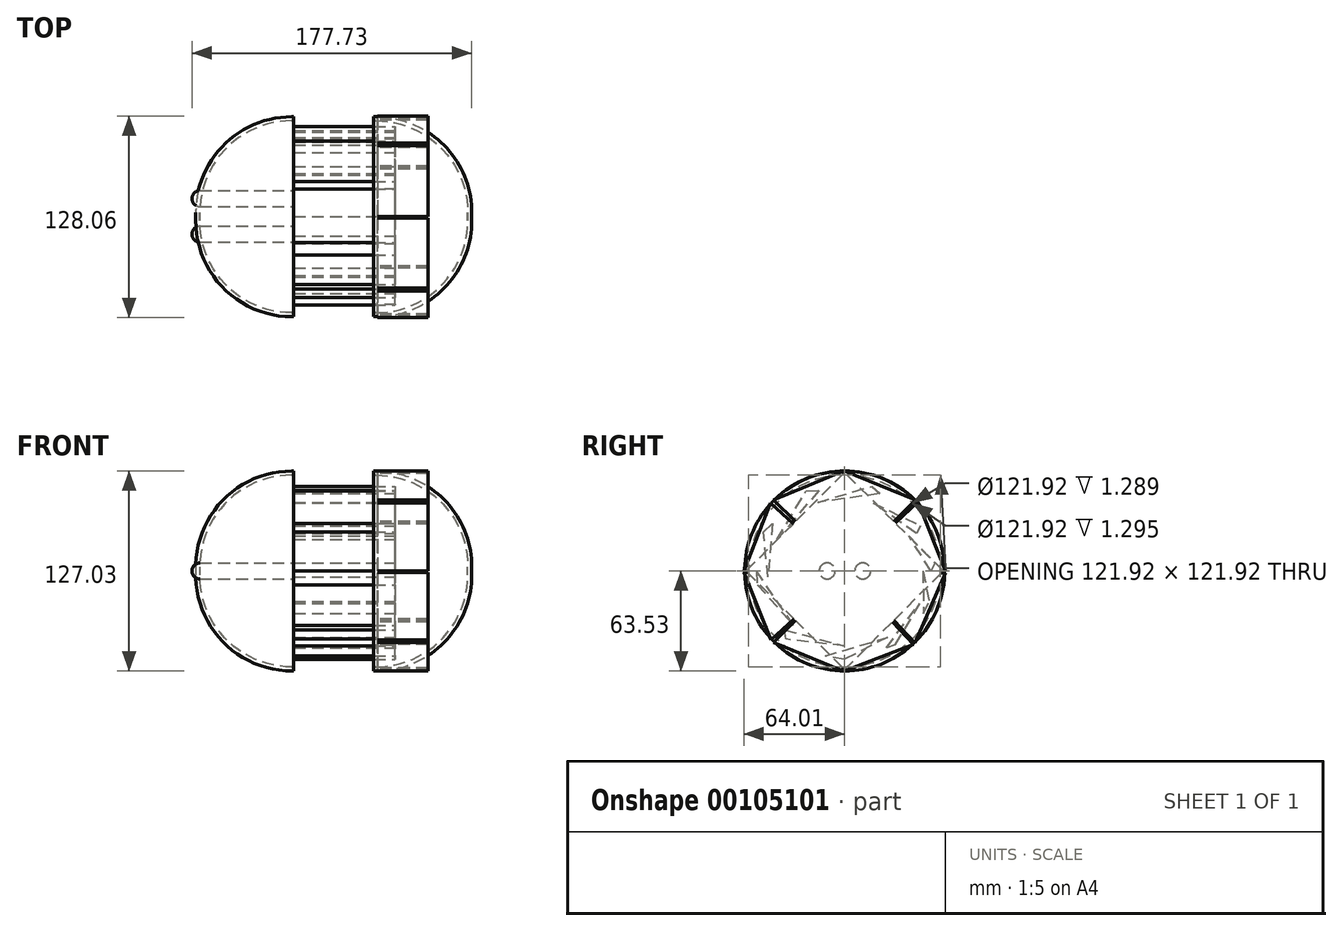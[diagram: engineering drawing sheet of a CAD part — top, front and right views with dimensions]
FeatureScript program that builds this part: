
annotation { "Feature Type Name" : "Feature", "Feature Type Description" : "" }
export const myFeature = defineFeature(function(context is Context, id is Id, definition is map)
    precondition{}
    {
        {
            var Q0;
            Q0=qCreatedBy(makeId("Right.planeOp"),FACE);
            var sketch = newSketch(context, id + "F0", { "sketchPlane" : qUnion([Q0])});
            skCircle(sketch, "E0", {"center": v(0, 0) * mm, "radius": 63.5 * mm});
            skSolve(sketch);
        }
        {
            var Q0;
            Q0=makeQuery(id+"F0.imprint","IMPRINT",FACE,{"disambiguationData":[TD([[makeQuery(id+"F0.imprint","IMPRINT",EDGE,{"derivedFrom":sQuery(id+"F0.wireOp",EDGE,"E0")}),1.0]])]});
            extrude(context, id + "F1", {"entities" : qUnion([Q0]), "depth" : 62.25 * mm});
        }
        {
            var Q0;
            Q0=makeQuery(id+"F1.opExtrude","CAP_FACE",FACE,{"disambiguationData":[OSD([sQuery(id+"F0.wireOp",EDGE,"E0")])],"isStart":false});
            fillet(context, id + "F2", {"entities" : qUnion([Q0]), "radius" : 60.96 * mm, "tangentPropagation" : true, "allowEdgeOverflow" : false});
        }
        {
            var Q0;
            Q0=makeQuery(id+"F1.opExtrude","CAP_FACE",FACE,{"disambiguationData":[OSD([sQuery(id+"F0.wireOp",EDGE,"E0")])],"isStart":true});
            shell(context, id + "F3", {"entities" : qUnion([Q0]), "thickness" : 2.54 * mm});
        }
        {
            var Q0;
            Q0=qCreatedBy(makeId("Right.planeOp"),FACE);
            var sketch = newSketch(context, id + "F4", { "sketchPlane" : qUnion([Q0])});
            skLineSegment(sketch, "E1", {"start": v(0, -56.04) * mm, "end": v(-12.28, -54.03) * mm});
            skLineSegment(sketch, "E2", {"start": v(-12.28, -54.03) * mm, "end": v(27.32, -42.1) * mm});
            skLineSegment(sketch, "E3", {"start": v(27.32, -42.1) * mm, "end": v(0, -56.04) * mm});
            skLineSegment(sketch, "E4", {"start": v(31.88, -46.96) * mm, "end": v(26.45, -48.8) * mm});
            skLineSegment(sketch, "E5", {"start": v(26.45, -48.8) * mm, "end": v(47.54, -20.5) * mm});
            skLineSegment(sketch, "E6", {"start": v(47.54, -20.5) * mm, "end": v(31.88, -46.96) * mm});
            skLineSegment(sketch, "E7", {"start": v(57.24, 5.09) * mm, "end": v(54.8, 0) * mm});
            skLineSegment(sketch, "E8", {"start": v(54.8, 0) * mm, "end": v(40.7, 22.26) * mm});
            skLineSegment(sketch, "E9", {"start": v(40.7, 22.26) * mm, "end": v(57.24, 5.09) * mm});
            skLineSegment(sketch, "E10", {"start": v(48.2, 28.62) * mm, "end": v(45.5, 23.93) * mm});
            skLineSegment(sketch, "E11", {"start": v(45.5, 23.93) * mm, "end": v(17.88, 43.35) * mm});
            skLineSegment(sketch, "E12", {"start": v(17.88, 43.35) * mm, "end": v(48.2, 28.62) * mm});
            skLineSegment(sketch, "E13", {"start": v(-17, 43.65) * mm, "end": v(17.47, 53.84) * mm});
            skLineSegment(sketch, "E14", {"start": v(50.17, -27.12) * mm, "end": v(53.75, -19.3) * mm});
            skLineSegment(sketch, "E15", {"start": v(49.71, 0) * mm, "end": v(50.17, -27.12) * mm});
            skLineSegment(sketch, "E16", {"start": v(49.71, 0) * mm, "end": v(53.75, -19.3) * mm});
            skLineSegment(sketch, "E17", {"start": v(-24.45, 50.84) * mm, "end": v(-16.35, 51.25) * mm});
            skLineSegment(sketch, "E18", {"start": v(-16.35, 51.25) * mm, "end": v(-42.93, 20.08) * mm});
            skLineSegment(sketch, "E19", {"start": v(-42.93, 20.08) * mm, "end": v(-24.45, 50.84) * mm});
            skLineSegment(sketch, "E20", {"start": v(-51.43, 24.68) * mm, "end": v(-45.8, 30.23) * mm});
            skLineSegment(sketch, "E21", {"start": v(-45.8, 30.23) * mm, "end": v(-48.78, -3.87) * mm});
            skLineSegment(sketch, "E22", {"start": v(-48.78, -3.87) * mm, "end": v(-51.43, 24.68) * mm});
            skLineSegment(sketch, "E23", {"start": v(-56.02, 0) * mm, "end": v(-55.43, -8.8) * mm});
            skLineSegment(sketch, "E24", {"start": v(-55.43, -8.8) * mm, "end": v(-32.43, -34.53) * mm});
            skLineSegment(sketch, "E25", {"start": v(-32.43, -34.53) * mm, "end": v(-56.02, 0) * mm});
            skLineSegment(sketch, "E26", {"start": v(-37.23, -43.3) * mm, "end": v(-38.28, -37.47) * mm});
            skLineSegment(sketch, "E27", {"start": v(-38.28, -37.47) * mm, "end": v(0, -47.56) * mm});
            skLineSegment(sketch, "E28", {"start": v(0, -47.56) * mm, "end": v(-37.23, -43.3) * mm});
            skLineSegment(sketch, "E29", {"start": v(17.47, 53.84) * mm, "end": v(22.3, 49.16) * mm});
            skLineSegment(sketch, "E30", {"start": v(22.3, 49.16) * mm, "end": v(-17, 43.65) * mm});
            skSolve(sketch);
        }
        {
            var Q0;
            Q0 = qSketchRegion(id + "F4", true);
            extrude(context, id + "F5", {"entities" : qUnion([Q0]), "oppositeDirection" : true, "depth" : 50.8 * mm, "hasSecondDirection" : true, "secondDirectionOppositeDirection" : false, "secondDirectionDepth" : 13.65 * mm});
        }
        {
            var Q0;
            Q0=qCreatedBy(makeId("Right.planeOp"),FACE);
            var sketch = newSketch(context, id + "F6", { "sketchPlane" : qUnion([Q0])});
            skLineSegment(sketch, "E31", {"start": v(-62.64, 0) * mm, "end": v(62.64, 0) * mm});
            skLineSegment(sketch, "E32", {"start": v(0, 62.64) * mm, "end": v(0, -62.64) * mm});
            skLineSegment(sketch, "E33", {"start": v(0, 62.64) * mm, "end": v(-62.64, 0) * mm});
            skLineSegment(sketch, "E34", {"start": v(-62.64, 0) * mm, "end": v(0, -62.64) * mm});
            skLineSegment(sketch, "E35", {"start": v(0, -62.64) * mm, "end": v(62.64, 0) * mm});
            skLineSegment(sketch, "E36", {"start": v(62.64, 0) * mm, "end": v(0, 62.64) * mm});
            skLineSegment(sketch, "E37", {"start": v(0, 0) * mm, "end": v(31.32, 31.32) * mm});
            skLineSegment(sketch, "E38", {"start": v(0, 0) * mm, "end": v(31.32, -31.32) * mm});
            skLineSegment(sketch, "E39", {"start": v(0, 0) * mm, "end": v(-31.32, -31.32) * mm});
            skLineSegment(sketch, "E40", {"start": v(0, 0) * mm, "end": v(-31.32, 31.32) * mm});
            skLineSegment(sketch, "E41", {"start": v(0, 0) * mm, "end": v(32.25, 30.38) * mm});
            skLineSegment(sketch, "E42", {"start": v(0, 0) * mm, "end": v(-0.84, 61.8) * mm});
            skLineSegment(sketch, "E43", {"start": v(0, 0) * mm, "end": v(-32.66, 29.98) * mm});
            skLineSegment(sketch, "E44", {"start": v(0, 0) * mm, "end": v(-61.8, -0.84) * mm});
            skLineSegment(sketch, "E45", {"start": v(0, 0) * mm, "end": v(-32.29, -30.35) * mm});
            skLineSegment(sketch, "E46", {"start": v(0, 0) * mm, "end": v(61.45, -1.18) * mm});
            skLineSegment(sketch, "E47", {"start": v(0, 0) * mm, "end": v(30.35, -32.29) * mm});
            skLineSegment(sketch, "E48", {"start": v(0, 0) * mm, "end": v(-1.18, -61.45) * mm});
            skLineSegment(sketch, "E49", {"start": v(31.32, 31.32) * mm, "end": v(45.12, 45.12) * mm});
            skLineSegment(sketch, "E50", {"start": v(32.25, 30.38) * mm, "end": v(46.64, 43.7) * mm});
            skLineSegment(sketch, "E51", {"start": v(46.64, 43.7) * mm, "end": v(45.12, 45.12) * mm});
            skLineSegment(sketch, "E52", {"start": v(62.64, 0) * mm, "end": v(64.03, 0) * mm});
            skLineSegment(sketch, "E53", {"start": v(61.45, -1.18) * mm, "end": v(64.05, -1.18) * mm});
            skLineSegment(sketch, "E54", {"start": v(64.05, -1.18) * mm, "end": v(64.03, 0) * mm});
            skLineSegment(sketch, "E55", {"start": v(31.32, -31.32) * mm, "end": v(44.72, -45.55) * mm});
            skLineSegment(sketch, "E56", {"start": v(30.35, -32.29) * mm, "end": v(43.79, -46.58) * mm});
            skLineSegment(sketch, "E57", {"start": v(43.79, -46.58) * mm, "end": v(44.72, -45.55) * mm});
            skLineSegment(sketch, "E58", {"start": v(0, -62.64) * mm, "end": v(0, -63.53) * mm});
            skLineSegment(sketch, "E59", {"start": v(-1.18, -61.45) * mm, "end": v(-1.18, -63.47) * mm});
            skLineSegment(sketch, "E60", {"start": v(0, -63.53) * mm, "end": v(-1.18, -63.47) * mm});
            skLineSegment(sketch, "E61", {"start": v(-31.32, -31.32) * mm, "end": v(-45.24, -45.24) * mm});
            skLineSegment(sketch, "E62", {"start": v(-32.29, -30.35) * mm, "end": v(-46.81, -43.66) * mm});
            skLineSegment(sketch, "E63", {"start": v(-46.81, -43.66) * mm, "end": v(-45.24, -45.24) * mm});
            skLineSegment(sketch, "E64", {"start": v(-62.64, 0) * mm, "end": v(-64, 0) * mm});
            skLineSegment(sketch, "E65", {"start": v(-61.8, -0.84) * mm, "end": v(-64, -0.84) * mm});
            skLineSegment(sketch, "E66", {"start": v(-64, -0.84) * mm, "end": v(-64, 0) * mm});
            skLineSegment(sketch, "E67", {"start": v(0, 62.64) * mm, "end": v(0, 63.46) * mm});
            skLineSegment(sketch, "E68", {"start": v(0, 63.46) * mm, "end": v(-0.84, 63.46) * mm});
            skLineSegment(sketch, "E69", {"start": v(-0.84, 63.46) * mm, "end": v(-0.84, 61.8) * mm});
            skLineSegment(sketch, "E70", {"start": v(-31.32, 31.32) * mm, "end": v(-45.15, 45.15) * mm});
            skLineSegment(sketch, "E71", {"start": v(-32.66, 29.98) * mm, "end": v(-47.07, 43.24) * mm});
            skLineSegment(sketch, "E72", {"start": v(-47.07, 43.24) * mm, "end": v(-45.15, 45.15) * mm});
            skLineSegment(sketch, "E73", {"start": v(-47.07, 43.24) * mm, "end": v(-64, 0) * mm});
            skLineSegment(sketch, "E74", {"start": v(-64, -0.84) * mm, "end": v(-46.81, -43.66) * mm});
            skLineSegment(sketch, "E75", {"start": v(-45.24, -45.24) * mm, "end": v(-1.18, -63.47) * mm});
            skLineSegment(sketch, "E76", {"start": v(0, -63.53) * mm, "end": v(43.79, -46.58) * mm});
            skLineSegment(sketch, "E77", {"start": v(44.72, -45.55) * mm, "end": v(64.05, -1.18) * mm});
            skLineSegment(sketch, "E78", {"start": v(64.03, 0) * mm, "end": v(46.64, 43.7) * mm});
            skLineSegment(sketch, "E79", {"start": v(45.12, 45.12) * mm, "end": v(0, 63.46) * mm});
            skLineSegment(sketch, "E80", {"start": v(-0.84, 63.46) * mm, "end": v(-45.15, 45.15) * mm});
            skSolve(sketch);
        }
        {
            var Q0;
            {var subQ2=sQuery(id+"F6.wireOp",EDGE,"E56");Q0=makeQuery(id+"F6.imprint","IMPRINT",FACE,{"disambiguationData":[TD([[makeQuery(id+"F6.imprint","IMPRINT",EDGE,{"derivedFrom":subQ2}),-1.0]])]});}
            var Q1;
            {var subQ2=sQuery(id+"F6.wireOp",EDGE,"E59");Q1=makeQuery(id+"F6.imprint","IMPRINT",FACE,{"disambiguationData":[TD([[makeQuery(id+"F6.imprint","IMPRINT",EDGE,{"derivedFrom":subQ2}),-1.0]])]});}
            var Q2;
            {var subQ2=sQuery(id+"F6.wireOp",EDGE,"E62");Q2=makeQuery(id+"F6.imprint","IMPRINT",FACE,{"disambiguationData":[TD([[makeQuery(id+"F6.imprint","IMPRINT",EDGE,{"derivedFrom":subQ2}),-1.0]])]});}
            var Q3;
            {var subQ2=sQuery(id+"F6.wireOp",EDGE,"E53");Q3=makeQuery(id+"F6.imprint","IMPRINT",FACE,{"disambiguationData":[TD([[makeQuery(id+"F6.imprint","IMPRINT",EDGE,{"derivedFrom":subQ2}),-1.0]])]});}
            var Q4;
            {var subQ2=sQuery(id+"F6.wireOp",EDGE,"E50");Q4=makeQuery(id+"F6.imprint","IMPRINT",FACE,{"disambiguationData":[TD([[makeQuery(id+"F6.imprint","IMPRINT",EDGE,{"derivedFrom":subQ2}),-1.0]])]});}
            var Q5;
            {var subQ2=sQuery(id+"F6.wireOp",EDGE,"E49");Q5=makeQuery(id+"F6.imprint","IMPRINT",FACE,{"disambiguationData":[TD([[makeQuery(id+"F6.imprint","IMPRINT",EDGE,{"derivedFrom":subQ2}),1.0]])]});}
            var Q6;
            {var subQ2=sQuery(id+"F6.wireOp",EDGE,"E69");Q6=makeQuery(id+"F6.imprint","IMPRINT",FACE,{"disambiguationData":[TD([[makeQuery(id+"F6.imprint","IMPRINT",EDGE,{"derivedFrom":subQ2}),-1.0]])]});}
            var Q7;
            {var subQ0=sQuery(id+"F6.wireOp",EDGE,"E64");Q7=makeQuery(id+"F6.imprint","IMPRINT",FACE,{"disambiguationData":[TD([[makeQuery(id+"F6.imprint","IMPRINT",EDGE,{"derivedFrom":subQ0}),-1.0]])]});}
            extrude(context, id + "F7", {"entities" : qUnion([Q0, Q1, Q2, Q3, Q4, Q5, Q6, Q7]), "depth" : 34.44 * mm, "hasSecondDirection" : true, "secondDirectionOppositeDirection" : false, "secondDirectionDepth" : 2.33 * mm});
        }
        {
            var Q0;
            Q0=makeQuery(id+"F5.opExtrude","CAP_FACE",FACE,{"disambiguationData":[OSD([sQuery(id+"F4.wireOp",EDGE,"E20"),sQuery(id+"F4.wireOp",EDGE,"E21"),sQuery(id+"F4.wireOp",EDGE,"E22")])],"isStart":false});
            var sketch = newSketch(context, id + "F8", { "sketchPlane" : qUnion([Q0])});
            skCircle(sketch, "E81", {"center": v(0, 0) * mm, "radius": 63.5 * mm});
            skSolve(sketch);
        }
        {
            var Q0;
            Q0 = qSketchRegion(id + "F8", true);
            extrude(context, id + "F9", {"entities" : qUnion([Q0]), "depth" : 62.26 * mm});
        }
        {
            var Q0;
            Q0=makeQuery(id+"F9.opExtrude","CAP_EDGE",EDGE,{"disambiguationData":[OSD([sQuery(id+"F8.wireOp",EDGE,"E81")])],"isStart":false});
            fillet(context, id + "F10", {"entities" : qUnion([Q0]), "radius" : 60.96 * mm, "tangentPropagation" : true, "allowEdgeOverflow" : false});
        }
        {
            var Q0;
            Q0=makeQuery(id+"F9.opExtrude","CAP_FACE",FACE,{"disambiguationData":[OSD([sQuery(id+"F8.wireOp",EDGE,"E81")])],"isStart":true});
            shell(context, id + "F11", {"entities" : qUnion([Q0]), "thickness" : 2.54 * mm});
        }
        {
            var Q0;
            Q0=makeQuery(id+"F5.opExtrude","CAP_FACE",FACE,{"disambiguationData":[OSD([sQuery(id+"F4.wireOp",EDGE,"E17"),sQuery(id+"F4.wireOp",EDGE,"E18"),sQuery(id+"F4.wireOp",EDGE,"E19")])],"isStart":false});
            var sketch = newSketch(context, id + "F12", { "sketchPlane" : qUnion([Q0])});
            skLineSegment(sketch, "E82", {"start": v(0, 0) * mm, "end": v(43.99, 0) * mm});
            skLineSegment(sketch, "E83", {"start": v(43.99, 0) * mm, "end": v(-43.99, 0) * mm});
            skCircle(sketch, "E84", {"center": v(-11.53, 0) * mm, "radius": 5.08 * mm});
            skCircle(sketch, "E85", {"center": v(11.14, 0) * mm, "radius": 5.08 * mm});
            skSolve(sketch);
        }
        {
            var Q0;
            Q0 = qSketchRegion(id + "F12", true);
            extrude(context, id + "F13", {"entities" : qUnion([Q0]), "depth" : 64.68 * mm});
        }
        {
            var Q0;
            Q0=makeQuery(id+"F13.opExtrude","CAP_EDGE",EDGE,{"disambiguationData":[OSD([sQuery(id+"F12.wireOp",EDGE,"E84")])],"isStart":false});
            var Q1;
            Q1=makeQuery(id+"F13.opExtrude","CAP_EDGE",EDGE,{"disambiguationData":[OSD([sQuery(id+"F12.wireOp",EDGE,"E85")])],"isStart":false});
            fillet(context, id + "F14", {"entities" : qUnion([Q0, Q1]), "radius" : 5.08 * mm, "tangentPropagation" : true, "allowEdgeOverflow" : false});
        }
    });
